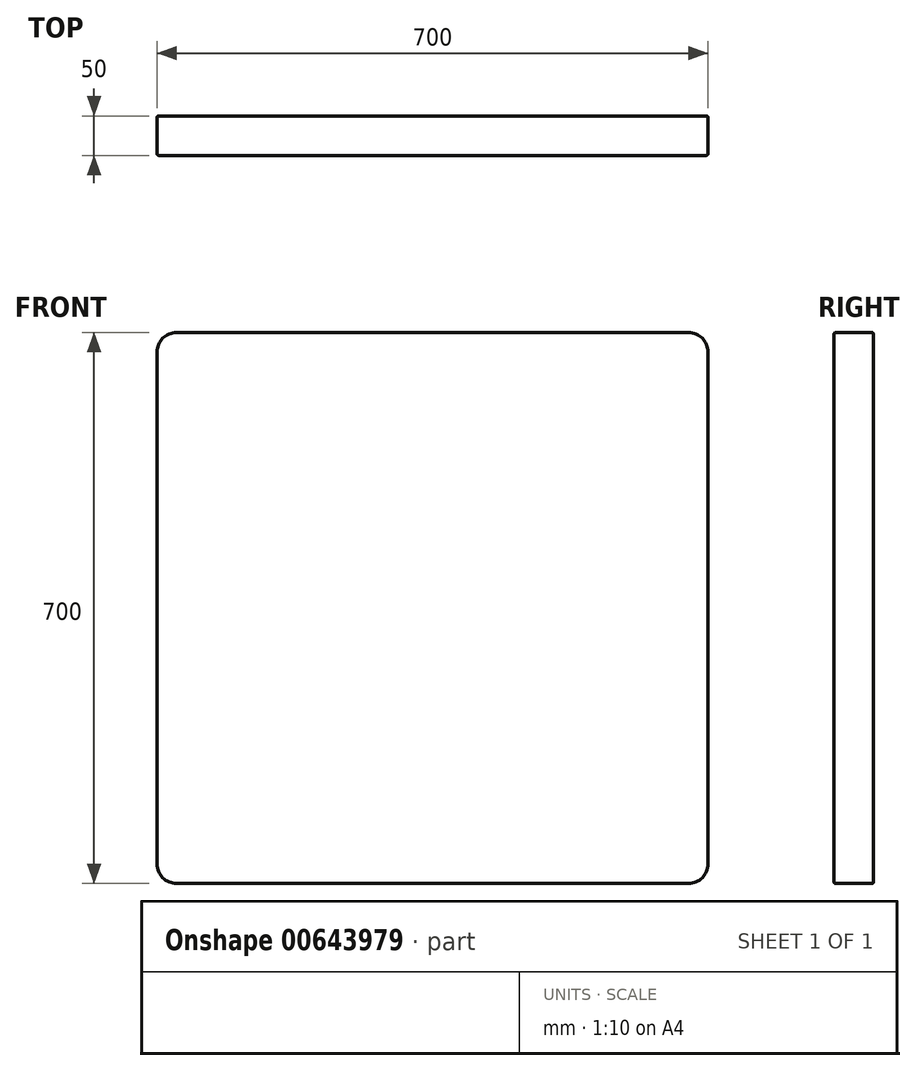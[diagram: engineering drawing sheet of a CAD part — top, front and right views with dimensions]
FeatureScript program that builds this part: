
annotation { "Feature Type Name" : "Feature", "Feature Type Description" : "" }
export const myFeature = defineFeature(function(context is Context, id is Id, definition is map)
    precondition{}
    {
        {
            var Q0;
            Q0=qCreatedBy(makeId("Front.planeOp"),FACE);
            var sketch = newSketch(context, id + "F0", { "sketchPlane" : qUnion([Q0])});
            skLineSegment(sketch, "E0.bottom", {"start": v(350, 350) * mm, "end": v(-350, 350) * mm});
            skLineSegment(sketch, "E0.top", {"start": v(350, -350) * mm, "end": v(-350, -350) * mm});
            skLineSegment(sketch, "E0.left", {"start": v(350, 350) * mm, "end": v(350, -350) * mm});
            skLineSegment(sketch, "E0.right", {"start": v(-350, 350) * mm, "end": v(-350, -350) * mm});
            skPoint(sketch, "E0.middle", {"position": v(0, 0) * mm});
            skSolve(sketch);
        }
        {
            var Q0;
            Q0 = qSketchRegion(id + "F0", true);
            extrude(context, id + "F1", {"entities" : qUnion([Q0]), "depth" : 50 * mm, "offsetDistance" : 25 * mm});
        }
        {
            var Q0;
            Q0=makeQuery(id+"F1.opExtrude","SWEPT_EDGE",EDGE,{"disambiguationData":[OSD([sQuery(id+"F0.wireOp",EDGE,"E0.bottom"),sQuery(id+"F0.wireOp",EDGE,"E0.right")])]});
            var Q1;
            Q1=makeQuery(id+"F1.opExtrude","SWEPT_EDGE",EDGE,{"disambiguationData":[OSD([sQuery(id+"F0.wireOp",EDGE,"E0.top"),sQuery(id+"F0.wireOp",EDGE,"E0.right")])]});
            var Q2;
            Q2=makeQuery(id+"F1.opExtrude","SWEPT_EDGE",EDGE,{"disambiguationData":[OSD([sQuery(id+"F0.wireOp",EDGE,"E0.top"),sQuery(id+"F0.wireOp",EDGE,"E0.left")])]});
            var Q3;
            Q3=makeQuery(id+"F1.opExtrude","SWEPT_EDGE",EDGE,{"disambiguationData":[OSD([sQuery(id+"F0.wireOp",EDGE,"E0.bottom"),sQuery(id+"F0.wireOp",EDGE,"E0.left")])]});
            fillet(context, id + "F2", {"entities" : qUnion([Q0, Q1, Q2, Q3]), "radius" : 25 * mm, "tangentPropagation" : true, "allowEdgeOverflow" : false});
        }
        {
            var Q0;
            Q0=makeQuery(id+"F1.opExtrude","CAP_EDGE",EDGE,{"disambiguationData":[OSD([sQuery(id+"F0.wireOp",EDGE,"E0.left")])],"isStart":false});
            var Q1;
            Q1=makeQuery(id+"F1.opExtrude","CAP_EDGE",EDGE,{"disambiguationData":[OSD([sQuery(id+"F0.wireOp",EDGE,"E0.bottom")])],"isStart":false});
            var Q2;
            Q2=makeQuery(id+"F1.opExtrude","CAP_EDGE",EDGE,{"disambiguationData":[OSD([sQuery(id+"F0.wireOp",EDGE,"E0.right")])],"isStart":false});
            var Q3;
            {var subQ0=sQuery(id+"F0.wireOp",EDGE,"E0.right");var subQ1=sQuery(id+"F0.wireOp",EDGE,"E0.bottom");Q3=makeQuery(id+"F2.opFillet","BLEND_EDGE",EDGE,{"blendedFrom":[makeQuery(id+"F1.opExtrude","SWEPT_EDGE",EDGE,{"disambiguationData":[OSD([subQ1,subQ0])]}),makeQuery(id+"F1.opExtrude","CAP_FACE",FACE,{"disambiguationData":[OSD([subQ1,sQuery(id+"F0.wireOp",EDGE,"E0.top"),sQuery(id+"F0.wireOp",EDGE,"E0.left"),subQ0])],"isStart":false})],"blendedInto":[makeQuery(id+"F1.opExtrude","CAP_FACE",FACE,{"disambiguationData":[OSD([subQ1,sQuery(id+"F0.wireOp",EDGE,"E0.top"),sQuery(id+"F0.wireOp",EDGE,"E0.left"),subQ0])],"isStart":false})]});}
            var Q4;
            {var subQ0=sQuery(id+"F0.wireOp",EDGE,"E0.right");var subQ1=sQuery(id+"F0.wireOp",EDGE,"E0.top");Q4=makeQuery(id+"F2.opFillet","BLEND_EDGE",EDGE,{"blendedFrom":[makeQuery(id+"F1.opExtrude","SWEPT_EDGE",EDGE,{"disambiguationData":[OSD([subQ1,subQ0])]}),makeQuery(id+"F1.opExtrude","CAP_FACE",FACE,{"disambiguationData":[OSD([sQuery(id+"F0.wireOp",EDGE,"E0.bottom"),subQ1,sQuery(id+"F0.wireOp",EDGE,"E0.left"),subQ0])],"isStart":false})],"blendedInto":[makeQuery(id+"F1.opExtrude","CAP_FACE",FACE,{"disambiguationData":[OSD([sQuery(id+"F0.wireOp",EDGE,"E0.bottom"),subQ1,sQuery(id+"F0.wireOp",EDGE,"E0.left"),subQ0])],"isStart":false})]});}
            var Q5;
            Q5=makeQuery(id+"F1.opExtrude","CAP_EDGE",EDGE,{"disambiguationData":[OSD([sQuery(id+"F0.wireOp",EDGE,"E0.top")])],"isStart":false});
            var Q6;
            {var subQ0=sQuery(id+"F0.wireOp",EDGE,"E0.left");var subQ1=sQuery(id+"F0.wireOp",EDGE,"E0.top");Q6=makeQuery(id+"F2.opFillet","BLEND_EDGE",EDGE,{"blendedFrom":[makeQuery(id+"F1.opExtrude","SWEPT_EDGE",EDGE,{"disambiguationData":[OSD([subQ1,subQ0])]}),makeQuery(id+"F1.opExtrude","CAP_FACE",FACE,{"disambiguationData":[OSD([sQuery(id+"F0.wireOp",EDGE,"E0.bottom"),subQ1,subQ0,sQuery(id+"F0.wireOp",EDGE,"E0.right")])],"isStart":false})],"blendedInto":[makeQuery(id+"F1.opExtrude","CAP_FACE",FACE,{"disambiguationData":[OSD([sQuery(id+"F0.wireOp",EDGE,"E0.bottom"),subQ1,subQ0,sQuery(id+"F0.wireOp",EDGE,"E0.right")])],"isStart":false})]});}
            var Q7;
            {var subQ0=sQuery(id+"F0.wireOp",EDGE,"E0.left");var subQ1=sQuery(id+"F0.wireOp",EDGE,"E0.bottom");Q7=makeQuery(id+"F2.opFillet","BLEND_EDGE",EDGE,{"blendedFrom":[makeQuery(id+"F1.opExtrude","SWEPT_EDGE",EDGE,{"disambiguationData":[OSD([subQ1,subQ0])]}),makeQuery(id+"F1.opExtrude","CAP_FACE",FACE,{"disambiguationData":[OSD([subQ1,sQuery(id+"F0.wireOp",EDGE,"E0.top"),subQ0,sQuery(id+"F0.wireOp",EDGE,"E0.right")])],"isStart":false})],"blendedInto":[makeQuery(id+"F1.opExtrude","CAP_FACE",FACE,{"disambiguationData":[OSD([subQ1,sQuery(id+"F0.wireOp",EDGE,"E0.top"),subQ0,sQuery(id+"F0.wireOp",EDGE,"E0.right")])],"isStart":false})]});}
            var Q8;
            Q8=makeQuery(id+"F1.opExtrude","CAP_EDGE",EDGE,{"disambiguationData":[OSD([sQuery(id+"F0.wireOp",EDGE,"E0.bottom")])],"isStart":true});
            var Q9;
            {var subQ0=sQuery(id+"F0.wireOp",EDGE,"E0.left");var subQ1=sQuery(id+"F0.wireOp",EDGE,"E0.bottom");Q9=makeQuery(id+"F2.opFillet","BLEND_EDGE",EDGE,{"blendedFrom":[makeQuery(id+"F1.opExtrude","SWEPT_EDGE",EDGE,{"disambiguationData":[OSD([subQ1,subQ0])]}),makeQuery(id+"F1.opExtrude","CAP_FACE",FACE,{"disambiguationData":[OSD([subQ1,sQuery(id+"F0.wireOp",EDGE,"E0.top"),subQ0,sQuery(id+"F0.wireOp",EDGE,"E0.right")])],"isStart":true})],"blendedInto":[makeQuery(id+"F1.opExtrude","CAP_FACE",FACE,{"disambiguationData":[OSD([subQ1,sQuery(id+"F0.wireOp",EDGE,"E0.top"),subQ0,sQuery(id+"F0.wireOp",EDGE,"E0.right")])],"isStart":true})]});}
            var Q10;
            Q10=makeQuery(id+"F1.opExtrude","CAP_EDGE",EDGE,{"disambiguationData":[OSD([sQuery(id+"F0.wireOp",EDGE,"E0.left")])],"isStart":true});
            var Q11;
            {var subQ0=sQuery(id+"F0.wireOp",EDGE,"E0.left");var subQ1=sQuery(id+"F0.wireOp",EDGE,"E0.top");Q11=makeQuery(id+"F2.opFillet","BLEND_EDGE",EDGE,{"blendedFrom":[makeQuery(id+"F1.opExtrude","SWEPT_EDGE",EDGE,{"disambiguationData":[OSD([subQ1,subQ0])]}),makeQuery(id+"F1.opExtrude","CAP_FACE",FACE,{"disambiguationData":[OSD([sQuery(id+"F0.wireOp",EDGE,"E0.bottom"),subQ1,subQ0,sQuery(id+"F0.wireOp",EDGE,"E0.right")])],"isStart":true})],"blendedInto":[makeQuery(id+"F1.opExtrude","CAP_FACE",FACE,{"disambiguationData":[OSD([sQuery(id+"F0.wireOp",EDGE,"E0.bottom"),subQ1,subQ0,sQuery(id+"F0.wireOp",EDGE,"E0.right")])],"isStart":true})]});}
            var Q12;
            Q12=makeQuery(id+"F1.opExtrude","CAP_EDGE",EDGE,{"disambiguationData":[OSD([sQuery(id+"F0.wireOp",EDGE,"E0.top")])],"isStart":true});
            var Q13;
            {var subQ0=sQuery(id+"F0.wireOp",EDGE,"E0.right");var subQ1=sQuery(id+"F0.wireOp",EDGE,"E0.top");Q13=makeQuery(id+"F2.opFillet","BLEND_EDGE",EDGE,{"blendedFrom":[makeQuery(id+"F1.opExtrude","SWEPT_EDGE",EDGE,{"disambiguationData":[OSD([subQ1,subQ0])]}),makeQuery(id+"F1.opExtrude","CAP_FACE",FACE,{"disambiguationData":[OSD([sQuery(id+"F0.wireOp",EDGE,"E0.bottom"),subQ1,sQuery(id+"F0.wireOp",EDGE,"E0.left"),subQ0])],"isStart":true})],"blendedInto":[makeQuery(id+"F1.opExtrude","CAP_FACE",FACE,{"disambiguationData":[OSD([sQuery(id+"F0.wireOp",EDGE,"E0.bottom"),subQ1,sQuery(id+"F0.wireOp",EDGE,"E0.left"),subQ0])],"isStart":true})]});}
            var Q14;
            Q14=makeQuery(id+"F1.opExtrude","CAP_EDGE",EDGE,{"disambiguationData":[OSD([sQuery(id+"F0.wireOp",EDGE,"E0.right")])],"isStart":true});
            var Q15;
            {var subQ0=sQuery(id+"F0.wireOp",EDGE,"E0.right");var subQ1=sQuery(id+"F0.wireOp",EDGE,"E0.bottom");Q15=makeQuery(id+"F2.opFillet","BLEND_EDGE",EDGE,{"blendedFrom":[makeQuery(id+"F1.opExtrude","SWEPT_EDGE",EDGE,{"disambiguationData":[OSD([subQ1,subQ0])]}),makeQuery(id+"F1.opExtrude","CAP_FACE",FACE,{"disambiguationData":[OSD([subQ1,sQuery(id+"F0.wireOp",EDGE,"E0.top"),sQuery(id+"F0.wireOp",EDGE,"E0.left"),subQ0])],"isStart":true})],"blendedInto":[makeQuery(id+"F1.opExtrude","CAP_FACE",FACE,{"disambiguationData":[OSD([subQ1,sQuery(id+"F0.wireOp",EDGE,"E0.top"),sQuery(id+"F0.wireOp",EDGE,"E0.left"),subQ0])],"isStart":true})]});}
            fillet(context, id + "F3", {"entities" : qUnion([Q0, Q1, Q2, Q3, Q4, Q5, Q6, Q7, Q8, Q9, Q10, Q11, Q12, Q13, Q14, Q15]), "radius" : 2 * mm, "tangentPropagation" : true, "allowEdgeOverflow" : false});
        }
    });
